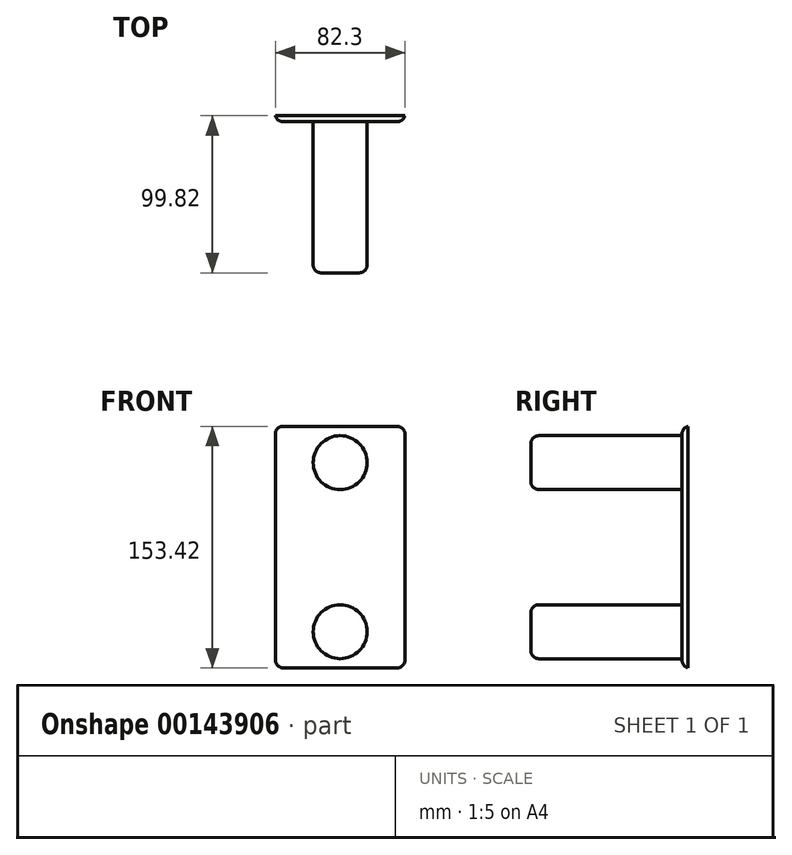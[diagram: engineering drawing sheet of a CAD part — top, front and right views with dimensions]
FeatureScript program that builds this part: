
annotation { "Feature Type Name" : "Feature", "Feature Type Description" : "" }
export const myFeature = defineFeature(function(context is Context, id is Id, definition is map)
    precondition{}
    {
        {
            var Q0;
            Q0=qCreatedBy(makeId("Front.planeOp"),FACE);
            var sketch = newSketch(context, id + "F0", { "sketchPlane" : qUnion([Q0])});
            skLineSegment(sketch, "E0.bottom", {"start": v(41.15, 76.7) * mm, "end": v(-41.15, 76.7) * mm});
            skLineSegment(sketch, "E0.top", {"start": v(41.15, -76.7) * mm, "end": v(-41.15, -76.7) * mm});
            skLineSegment(sketch, "E0.left", {"start": v(41.15, 76.7) * mm, "end": v(41.15, -76.7) * mm});
            skLineSegment(sketch, "E0.right", {"start": v(-41.15, 76.7) * mm, "end": v(-41.15, -76.7) * mm});
            skPoint(sketch, "E0.middle", {"position": v(0, 0) * mm});
            skSolve(sketch);
        }
        {
            var Q0;
            Q0 = qSketchRegion(id + "F0", true);
            extrude(context, id + "F1", {"entities" : qUnion([Q0]), "depth" : 3.8 * mm});
        }
        {
            var Q0;
            Q0=makeQuery(id+"F1.opExtrude","CAP_FACE",FACE,{"disambiguationData":[OSD([sQuery(id+"F0.wireOp",EDGE,"E0.bottom"),sQuery(id+"F0.wireOp",EDGE,"E0.top"),sQuery(id+"F0.wireOp",EDGE,"E0.left"),sQuery(id+"F0.wireOp",EDGE,"E0.right")])],"isStart":false});
            var sketch = newSketch(context, id + "F2", { "sketchPlane" : qUnion([Q0])});
            skSolve(sketch);
        }
        {
            var Q0;
            Q0=makeQuery(id+"F2.imprint","IMPRINT",FACE,{"disambiguationData":[TD([[makeQuery(id+"F2.imprint","IMPRINT",EDGE,{"derivedFrom":makeQuery(id+"F1.opExtrude","CAP_EDGE",EDGE,{"disambiguationData":[OSD([sQuery(id+"F0.wireOp",EDGE,"E0.bottom")])],"isStart":false})}),1.0]])]});
            var sketch = newSketch(context, id + "F3", { "sketchPlane" : qUnion([Q0])});
            skCircle(sketch, "E1", {"center": v(0, 53.61) * mm, "radius": 17.15 * mm});
            skSolve(sketch);
        }
        {
            var Q0;
            Q0=makeQuery(id+"F2.imprint","IMPRINT",FACE,{"disambiguationData":[TD([[makeQuery(id+"F2.imprint","IMPRINT",EDGE,{"derivedFrom":makeQuery(id+"F1.opExtrude","CAP_EDGE",EDGE,{"disambiguationData":[OSD([sQuery(id+"F0.wireOp",EDGE,"E0.bottom")])],"isStart":false})}),1.0]])]});
            var sketch = newSketch(context, id + "F4", { "sketchPlane" : qUnion([Q0])});
            skCircle(sketch, "E2", {"center": v(0, -53.75) * mm, "radius": 17.14 * mm});
            skSolve(sketch);
        }
        {
            var Q0;
            Q0 = qSketchRegion(id + "F3", true);
            extrude(context, id + "F5", {"entities" : qUnion([Q0]), "operationType" : NewBodyOperationType.ADD, "depth" : 96.01 * mm});
        }
        {
            var Q0;
            Q0 = qSketchRegion(id + "F4", true);
            extrude(context, id + "F6", {"entities" : qUnion([Q0]), "operationType" : NewBodyOperationType.ADD, "depth" : 96.01 * mm});
        }
        {
            var Q0;
            Q0=makeQuery(id+"F5.opExtrude","CAP_EDGE",EDGE,{"disambiguationData":[OSD([sQuery(id+"F3.wireOp",EDGE,"E1")])],"isStart":false});
            var Q1;
            Q1=makeQuery(id+"F5.opExtrude","CAP_EDGE",EDGE,{"disambiguationData":[OSD([sQuery(id+"F3.wireOp",EDGE,"E1")])],"isStart":true});
            var Q2;
            Q2=makeQuery(id+"F6.opExtrude","CAP_EDGE",EDGE,{"disambiguationData":[OSD([sQuery(id+"F4.wireOp",EDGE,"E2")])],"isStart":true});
            var Q3;
            Q3=makeQuery(id+"F6.opExtrude","CAP_FACE",FACE,{"disambiguationData":[OSD([sQuery(id+"F4.wireOp",EDGE,"E2")])],"isStart":false});
            fillet(context, id + "F7", {"entities" : qUnion([Q0, Q1, Q2, Q3]), "radius" : 5.08 * mm, "tangentPropagation" : true, "allowEdgeOverflow" : false});
        }
        {
            var Q0;
            Q0=makeQuery(id+"F1.opExtrude","CAP_EDGE",EDGE,{"disambiguationData":[OSD([sQuery(id+"F0.wireOp",EDGE,"E0.bottom")])],"isStart":false});
            var Q1;
            Q1=makeQuery(id+"F1.opExtrude","CAP_EDGE",EDGE,{"disambiguationData":[OSD([sQuery(id+"F0.wireOp",EDGE,"E0.right")])],"isStart":false});
            var Q2;
            Q2=makeQuery(id+"F1.opExtrude","CAP_EDGE",EDGE,{"disambiguationData":[OSD([sQuery(id+"F0.wireOp",EDGE,"E0.left")])],"isStart":false});
            var Q3;
            Q3=makeQuery(id+"F1.opExtrude","CAP_EDGE",EDGE,{"disambiguationData":[OSD([sQuery(id+"F0.wireOp",EDGE,"E0.top")])],"isStart":false});
            fillet(context, id + "F8", {"entities" : qUnion([Q0, Q1, Q2, Q3]), "radius" : 5.08 * mm, "tangentPropagation" : true, "allowEdgeOverflow" : false});
        }
        {
            var Q0;
            Q0=makeQuery(id+"F8.opFillet","BLEND_EDGE",EDGE,{"blendedFrom":[makeQuery(id+"F1.opExtrude","CAP_EDGE",EDGE,{"disambiguationData":[OSD([sQuery(id+"F0.wireOp",EDGE,"E0.bottom")])],"isStart":false}),makeQuery(id+"F1.opExtrude","CAP_EDGE",EDGE,{"disambiguationData":[OSD([sQuery(id+"F0.wireOp",EDGE,"E0.right")])],"isStart":false})],"blendedInto":[]});
            var Q1;
            Q1=makeQuery(id+"F8.opFillet","BLEND_EDGE",EDGE,{"blendedFrom":[makeQuery(id+"F1.opExtrude","CAP_EDGE",EDGE,{"disambiguationData":[OSD([sQuery(id+"F0.wireOp",EDGE,"E0.bottom")])],"isStart":false}),makeQuery(id+"F1.opExtrude","CAP_EDGE",EDGE,{"disambiguationData":[OSD([sQuery(id+"F0.wireOp",EDGE,"E0.left")])],"isStart":false})],"blendedInto":[]});
            var Q2;
            Q2=makeQuery(id+"F8.opFillet","BLEND_EDGE",EDGE,{"blendedFrom":[makeQuery(id+"F1.opExtrude","CAP_EDGE",EDGE,{"disambiguationData":[OSD([sQuery(id+"F0.wireOp",EDGE,"E0.top")])],"isStart":false}),makeQuery(id+"F1.opExtrude","CAP_EDGE",EDGE,{"disambiguationData":[OSD([sQuery(id+"F0.wireOp",EDGE,"E0.left")])],"isStart":false})],"blendedInto":[]});
            var Q3;
            Q3=makeQuery(id+"F8.opFillet","BLEND_EDGE",EDGE,{"blendedFrom":[makeQuery(id+"F1.opExtrude","CAP_EDGE",EDGE,{"disambiguationData":[OSD([sQuery(id+"F0.wireOp",EDGE,"E0.top")])],"isStart":false}),makeQuery(id+"F1.opExtrude","CAP_EDGE",EDGE,{"disambiguationData":[OSD([sQuery(id+"F0.wireOp",EDGE,"E0.right")])],"isStart":false})],"blendedInto":[]});
            fillet(context, id + "F9", {"entities" : qUnion([Q0, Q1, Q2, Q3]), "radius" : 5.08 * mm, "tangentPropagation" : true, "allowEdgeOverflow" : false});
        }
    });
